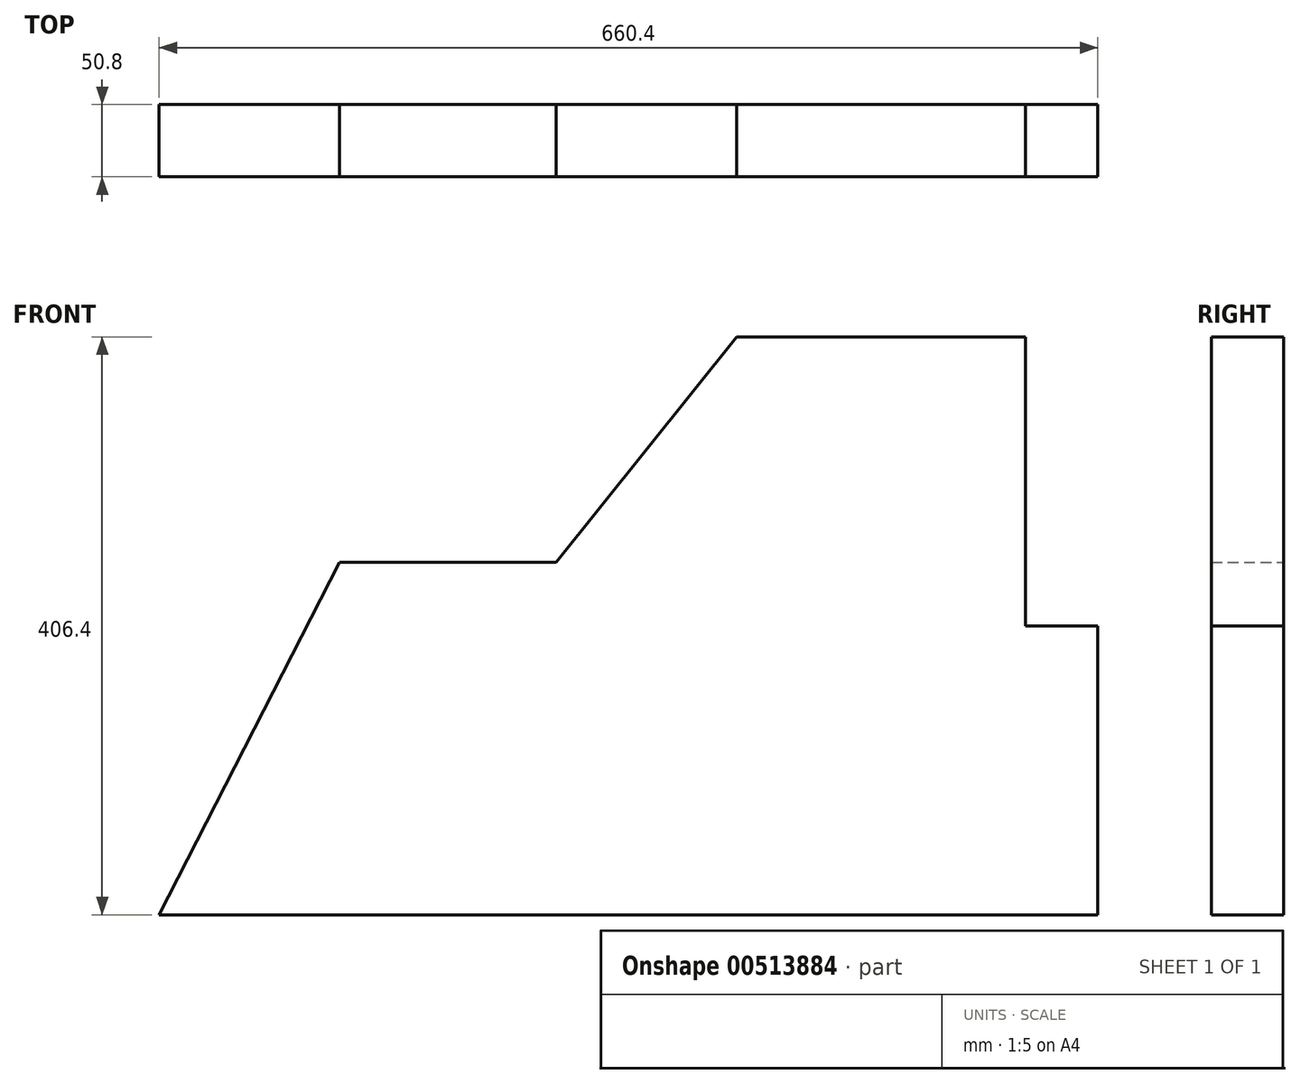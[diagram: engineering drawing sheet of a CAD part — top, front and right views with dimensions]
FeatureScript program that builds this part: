
annotation { "Feature Type Name" : "Feature", "Feature Type Description" : "" }
export const myFeature = defineFeature(function(context is Context, id is Id, definition is map)
    precondition{}
    {
        {
            var Q0;
            Q0=qCreatedBy(makeId("Front.planeOp"),FACE);
            var sketch = newSketch(context, id + "F0", { "sketchPlane" : qUnion([Q0])});
            skLineSegment(sketch, "E0", {"start": v(1, -62.07) * mm, "end": v(661.4, -62.07) * mm});
            skLineSegment(sketch, "E1", {"start": v(661.4, -62.07) * mm, "end": v(661.4, 141.13) * mm});
            skLineSegment(sketch, "E2", {"start": v(661.4, 141.13) * mm, "end": v(610.6, 141.13) * mm});
            skLineSegment(sketch, "E3", {"start": v(610.6, 141.13) * mm, "end": v(610.6, 344.33) * mm});
            skLineSegment(sketch, "E4", {"start": v(610.6, 344.33) * mm, "end": v(407.4, 344.33) * mm});
            skLineSegment(sketch, "E5", {"start": v(280.4, 185.7) * mm, "end": v(128, 185.7) * mm});
            skLineSegment(sketch, "E6", {"start": v(128, 185.7) * mm, "end": v(1, -62.07) * mm});
            skLineSegment(sketch, "E7", {"start": v(407.4, 344.33) * mm, "end": v(280.4, 185.7) * mm});
            skSolve(sketch);
        }
        {
            var Q0;
            Q0=makeQuery(id+"F0.imprint","IMPRINT",FACE,{"disambiguationData":[TD([[makeQuery(id+"F0.imprint","IMPRINT",EDGE,{"derivedFrom":sQuery(id+"F0.wireOp",EDGE,"E0")}),1.0]])]});
            extrude(context, id + "F1", {"entities" : qUnion([Q0]), "depth" : 50.8 * mm, "offsetDistance" : 25.4 * mm});
        }
    });
